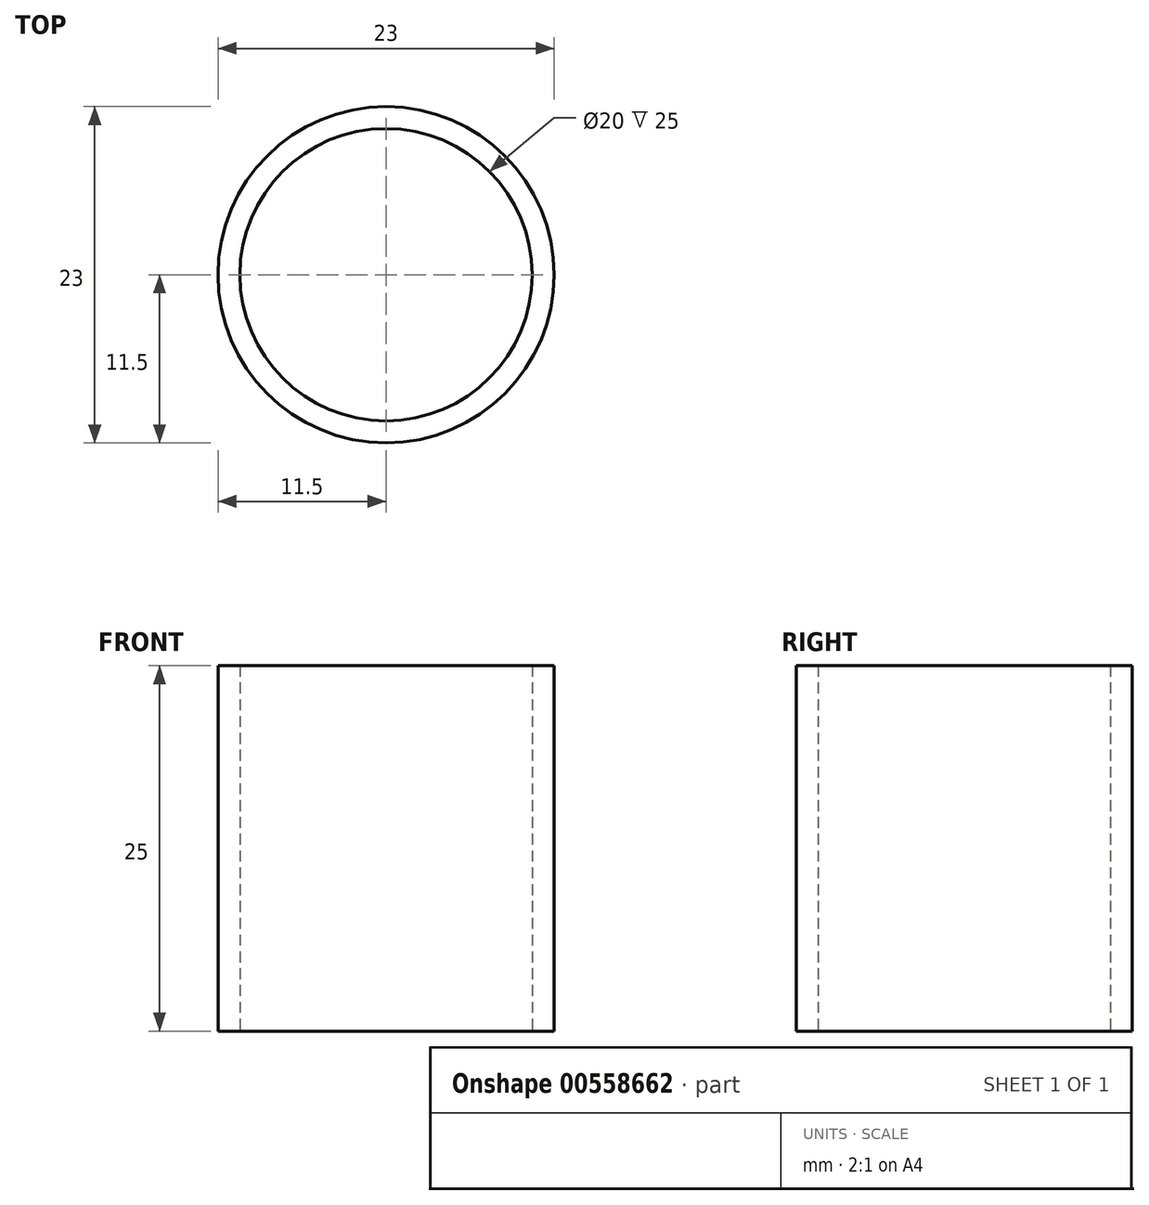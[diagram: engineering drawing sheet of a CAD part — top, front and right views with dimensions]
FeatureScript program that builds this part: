
annotation { "Feature Type Name" : "Feature", "Feature Type Description" : "" }
export const myFeature = defineFeature(function(context is Context, id is Id, definition is map)
    precondition{}
    {
        {
            var Q0;
            Q0=qCreatedBy(makeId("Top.planeOp"),FACE);
            var sketch = newSketch(context, id + "F0", { "sketchPlane" : qUnion([Q0])});
            skCircle(sketch, "E0", {"center": v(0, 0) * mm, "radius": 11.5 * mm});
            skCircle(sketch, "E1", {"center": v(0, 0) * mm, "radius": 10 * mm});
            skSolve(sketch);
        }
        {
            var Q0;
            Q0 = qSketchRegion(id + "F0", true);
            extrude(context, id + "F1", {"entities" : qUnion([Q0]), "depth" : 25 * mm, "offsetDistance" : 25 * mm});
        }
    });
